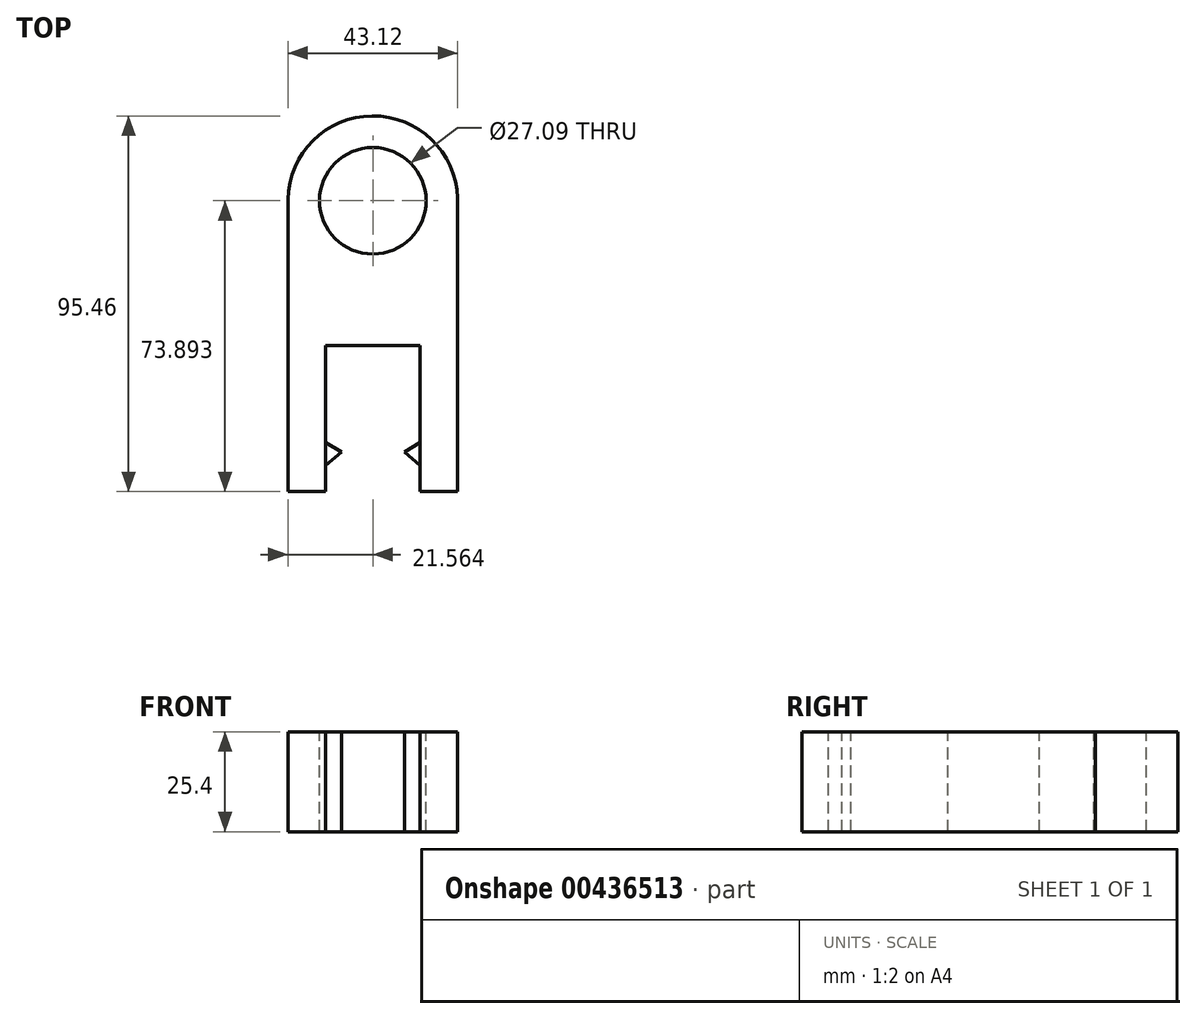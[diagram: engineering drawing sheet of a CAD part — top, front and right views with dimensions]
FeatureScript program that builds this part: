
annotation { "Feature Type Name" : "Feature", "Feature Type Description" : "" }
export const myFeature = defineFeature(function(context is Context, id is Id, definition is map)
    precondition{}
    {
        {
            var Q0;
            Q0=qCreatedBy(makeId("Top.planeOp"),FACE);
            var sketch = newSketch(context, id + "F0", { "sketchPlane" : qUnion([Q0])});
            skLineSegment(sketch, "E0.bottom", {"start": v(21.56, 47.73) * mm, "end": v(-21.56, 47.73) * mm});
            skLineSegment(sketch, "E0.top", {"start": v(21.56, -47.73) * mm, "end": v(-21.56, -47.73) * mm});
            skLineSegment(sketch, "E0.left", {"start": v(21.56, 47.73) * mm, "end": v(21.56, -47.73) * mm});
            skLineSegment(sketch, "E0.right", {"start": v(-21.56, 47.73) * mm, "end": v(-21.56, -47.73) * mm});
            skPoint(sketch, "E0.middle", {"position": v(0, 0) * mm});
            skSolve(sketch);
        }
        {
            var Q0;
            Q0 = qSketchRegion(id + "F0", true);
            extrude(context, id + "F1", {"entities" : qUnion([Q0]), "depth" : 25.4 * mm});
        }
        {
            var Q0;
            Q0=makeQuery(id+"F1.opExtrude","CAP_FACE",FACE,{"disambiguationData":[OSD([sQuery(id+"F0.wireOp",EDGE,"E0.bottom"),sQuery(id+"F0.wireOp",EDGE,"E0.top"),sQuery(id+"F0.wireOp",EDGE,"E0.left"),sQuery(id+"F0.wireOp",EDGE,"E0.right")])],"isStart":false});
            var sketch = newSketch(context, id + "F2", { "sketchPlane" : qUnion([Q0])});
            skLineSegment(sketch, "E1.bottom", {"start": v(-12.04, -10.61) * mm, "end": v(12.02, -10.61) * mm});
            skLineSegment(sketch, "E1.top", {"start": v(-12.04, -47.73) * mm, "end": v(12.02, -47.73) * mm});
            skLineSegment(sketch, "E1.left", {"start": v(-12.04, -10.61) * mm, "end": v(-12.04, -47.73) * mm});
            skLineSegment(sketch, "E1.right", {"start": v(12.02, -10.61) * mm, "end": v(12.02, -47.73) * mm});
            skSolve(sketch);
        }
        {
            var Q0;
            Q0 = qSketchRegion(id + "F2", true);
            extrude(context, id + "F3", {"entities" : qUnion([Q0]), "operationType" : NewBodyOperationType.REMOVE, "oppositeDirection" : true, "depth" : 25.4 * mm});
        }
        {
            var Q0;
            Q0=makeQuery(id+"F1.opExtrude","CAP_FACE",FACE,{"disambiguationData":[OSD([sQuery(id+"F0.wireOp",EDGE,"E0.bottom"),sQuery(id+"F0.wireOp",EDGE,"E0.top"),sQuery(id+"F0.wireOp",EDGE,"E0.left"),sQuery(id+"F0.wireOp",EDGE,"E0.right")])],"isStart":false});
            var sketch = newSketch(context, id + "F4", { "sketchPlane" : qUnion([Q0])});
            skCircle(sketch, "E2", {"center": v(0, 26.16) * mm, "radius": 21.57 * mm});
            skPoint(sketch, "E2.first.point", {"position": v(-21.56, 25.85) * mm});
            skPoint(sketch, "E2.second.point", {"position": v(0, 47.73) * mm});
            skPoint(sketch, "E2.third.point", {"position": v(21.56, 25.5) * mm});
            skLineSegment(sketch, "E3", {"start": v(-21.56, 47.73) * mm, "end": v(-21.56, 25.85) * mm});
            skLineSegment(sketch, "E4", {"start": v(-21.56, 47.73) * mm, "end": v(0, 47.73) * mm});
            skLineSegment(sketch, "E5", {"start": v(0, 47.73) * mm, "end": v(21.56, 47.73) * mm});
            skLineSegment(sketch, "E6", {"start": v(21.56, 47.73) * mm, "end": v(21.56, 25.5) * mm});
            skLineSegment(sketch, "E7", {"start": v(-21.56, 25.85) * mm, "end": v(21.56, 25.5) * mm});
            skCircle(sketch, "E8", {"center": v(0, 26.16) * mm, "radius": 13.54 * mm});
            skSolve(sketch);
        }
        {
            var Q0;
            {var subQ0=sQuery(id+"F4.wireOp",EDGE,"E4");Q0=makeQuery(id+"F4.imprint","IMPRINT",FACE,{"disambiguationData":[TD([[makeQuery(id+"F4.imprint","IMPRINT",EDGE,{"derivedFrom":subQ0}),1.0]])]});}
            var Q1;
            {var subQ0=sQuery(id+"F4.wireOp",EDGE,"E5");Q1=makeQuery(id+"F4.imprint","IMPRINT",FACE,{"disambiguationData":[TD([[makeQuery(id+"F4.imprint","IMPRINT",EDGE,{"derivedFrom":subQ0}),1.0]])]});}
            var Q2;
            {var subQ0=sQuery(id+"F4.wireOp",EDGE,"E8");var subQ1=sQuery(id+"F4.wireOp",EDGE,"E7");var subQ2=makeQuery(id+"F4.imprint","INTERSECT",VERTEX,{"disambiguationData":[OD(0.0)],"derivedFrom":[subQ1,subQ0]});Q2=makeQuery(id+"F4.imprint","IMPRINT",FACE,{"disambiguationData":[TD([[makeQuery(id+"F4.imprint","IMPRINT",EDGE,{"disambiguationData":[TD([[subQ2,-1.0]])],"derivedFrom":subQ1}),1.0]])]});}
            var Q3;
            {var subQ0=sQuery(id+"F4.wireOp",EDGE,"E8");var subQ1=sQuery(id+"F4.wireOp",EDGE,"E7");var subQ2=makeQuery(id+"F4.imprint","INTERSECT",VERTEX,{"disambiguationData":[OD(0.0)],"derivedFrom":[subQ1,subQ0]});Q3=makeQuery(id+"F4.imprint","IMPRINT",FACE,{"disambiguationData":[TD([[makeQuery(id+"F4.imprint","IMPRINT",EDGE,{"disambiguationData":[TD([[subQ2,-1.0]])],"derivedFrom":subQ1}),-1.0]])]});}
            extrude(context, id + "F5", {"entities" : qUnion([Q0, Q1, Q2, Q3]), "operationType" : NewBodyOperationType.REMOVE, "oppositeDirection" : true, "depth" : 25.4 * mm});
        }
        {
            var Q0;
            Q0=makeQuery(id+"F1.opExtrude","CAP_FACE",FACE,{"disambiguationData":[OSD([sQuery(id+"F0.wireOp",EDGE,"E0.bottom"),sQuery(id+"F0.wireOp",EDGE,"E0.top"),sQuery(id+"F0.wireOp",EDGE,"E0.left"),sQuery(id+"F0.wireOp",EDGE,"E0.right")])],"isStart":false});
            var sketch = newSketch(context, id + "F6", { "sketchPlane" : qUnion([Q0])});
            skLineSegment(sketch, "E9", {"start": v(-12.04, -41.07) * mm, "end": v(-8, -37.65) * mm});
            skLineSegment(sketch, "E10", {"start": v(-8, -37.65) * mm, "end": v(-8, -37.65) * mm});
            skLineSegment(sketch, "E11", {"start": v(-12.04, -35.27) * mm, "end": v(-8, -37.65) * mm});
            skLineSegment(sketch, "E12", {"start": v(0, -24.55) * mm, "end": v(0, -42.77) * mm});
            skLineSegment(sketch, "E13.MirrorCS", {"start": v(12.04, -35.27) * mm, "end": v(8, -37.65) * mm});
            skLineSegment(sketch, "E14.MirrorCS", {"start": v(12.04, -41.07) * mm, "end": v(8, -37.65) * mm});
            skLineSegment(sketch, "E15", {"start": v(-12.04, -35.27) * mm, "end": v(-12.04, -41.07) * mm});
            skLineSegment(sketch, "E16.MirrorCS", {"start": v(12.04, -35.27) * mm, "end": v(12.04, -41.07) * mm});
            skSolve(sketch);
        }
        {
            var Q0;
            Q0=makeQuery(id+"F6.imprint","IMPRINT",FACE,{"disambiguationData":[TD([[makeQuery(id+"F6.imprint","IMPRINT",EDGE,{"derivedFrom":sQuery(id+"F6.wireOp",EDGE,"E9")}),1.0]])]});
            var Q1;
            {var subQ0=sQuery(id+"F6.wireOp",EDGE,"E14.MirrorCS");var subQ1=sQuery(id+"F6.wireOp",EDGE,"E13.MirrorCS");var subQ2=makeQuery(id+"F6.imprint","INTERSECT",VERTEX,{"derivedFrom":[subQ1,subQ0]});Q1=makeQuery(id+"F6.imprint","IMPRINT",FACE,{"disambiguationData":[TD([[makeQuery(id+"F6.imprint","IMPRINT",EDGE,{"disambiguationData":[TD([[subQ2,1.0]])],"derivedFrom":subQ1}),1.0]])]});}
            extrude(context, id + "F7", {"entities" : qUnion([Q0, Q1]), "oppositeDirection" : true, "depth" : 25.4 * mm});
        }
    });
